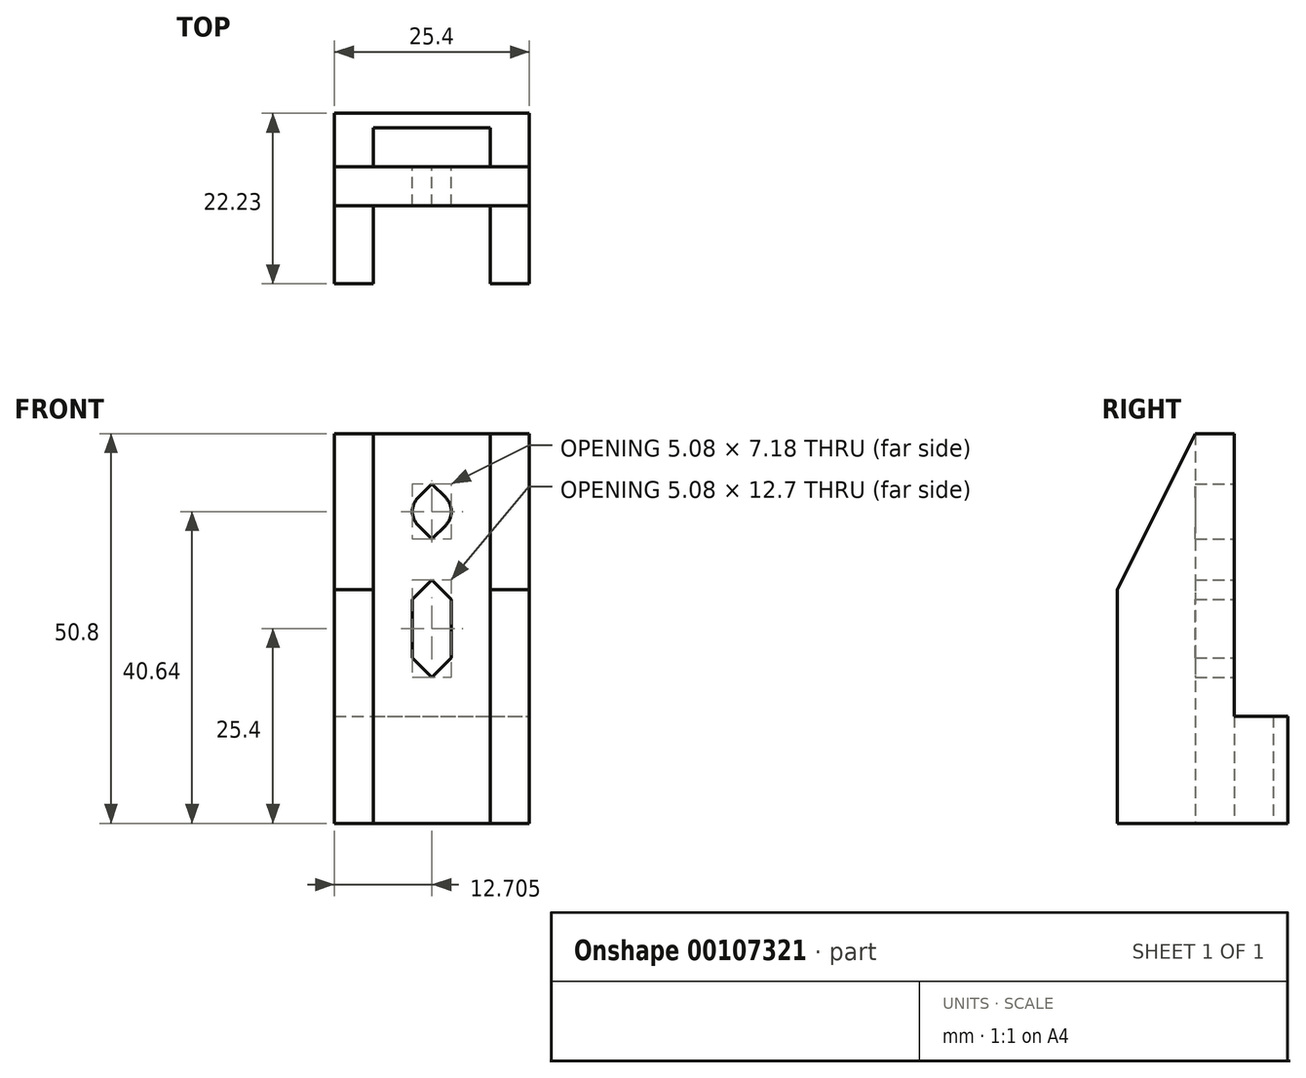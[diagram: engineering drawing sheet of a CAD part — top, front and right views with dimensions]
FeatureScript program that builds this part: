
annotation { "Feature Type Name" : "Feature", "Feature Type Description" : "" }
export const myFeature = defineFeature(function(context is Context, id is Id, definition is map)
    precondition{}
    {
        {
            var Q0;
            Q0=qCreatedBy(makeId("Top.planeOp"),FACE);
            var sketch = newSketch(context, id + "F0", { "sketchPlane" : qUnion([Q0])});
            skLineSegment(sketch, "E0.bottom", {"start": v(-5.07, -11.68) * mm, "end": v(10.17, -11.68) * mm});
            skLineSegment(sketch, "E0.top", {"start": v(-5.07, -6.6) * mm, "end": v(10.17, -6.6) * mm});
            skLineSegment(sketch, "E0.left", {"start": v(-5.07, -11.68) * mm, "end": v(-5.07, -6.6) * mm});
            skLineSegment(sketch, "E0.right", {"start": v(10.17, -11.68) * mm, "end": v(10.17, -6.6) * mm});
            skLineSegment(sketch, "E1.bottom", {"start": v(-10.15, -16.76) * mm, "end": v(15.25, -16.76) * mm});
            skLineSegment(sketch, "E1.top", {"start": v(-10.15, -4.7) * mm, "end": v(15.25, -4.7) * mm});
            skLineSegment(sketch, "E1.left", {"start": v(-10.15, -16.76) * mm, "end": v(-10.15, -4.7) * mm});
            skLineSegment(sketch, "E1.right", {"start": v(15.25, -16.76) * mm, "end": v(15.25, -4.7) * mm});
            skSolve(sketch);
        }
        {
            var Q0;
            Q0=makeQuery(id+"F0.imprint","IMPRINT",FACE,{"disambiguationData":[TD([[makeQuery(id+"F0.imprint","IMPRINT",EDGE,{"derivedFrom":sQuery(id+"F0.wireOp",EDGE,"E0.bottom")}),-1.0]])]});
            extrude(context, id + "F1", {"entities" : qUnion([Q0]), "depth" : 101.6 * mm});
        }
        {
            var Q0;
            Q0=qCreatedBy(makeId("Top.planeOp"),FACE);
            var sketch = newSketch(context, id + "F6", { "sketchPlane" : qUnion([Q0])});
            skLineSegment(sketch, "E2.bottom", {"start": v(-10.15, -16.76) * mm, "end": v(-5.07, -16.76) * mm});
            skLineSegment(sketch, "E2.top", {"start": v(-10.15, -26.92) * mm, "end": v(-5.07, -26.92) * mm});
            skLineSegment(sketch, "E2.left", {"start": v(-10.15, -16.76) * mm, "end": v(-10.15, -26.92) * mm});
            skLineSegment(sketch, "E2.right", {"start": v(-5.07, -16.76) * mm, "end": v(-5.07, -26.92) * mm});
            skLineSegment(sketch, "E3.bottom", {"start": v(15.25, -16.76) * mm, "end": v(10.17, -16.76) * mm});
            skLineSegment(sketch, "E3.top", {"start": v(15.25, -26.92) * mm, "end": v(10.17, -26.92) * mm});
            skLineSegment(sketch, "E3.left", {"start": v(15.25, -16.76) * mm, "end": v(15.25, -26.92) * mm});
            skLineSegment(sketch, "E3.right", {"start": v(10.17, -16.76) * mm, "end": v(10.17, -26.92) * mm});
            skSolve(sketch);
        }
        {
            var Q0;
            Q0 = qSketchRegion(id + "F6", true);
            var Q1;
            Q1=makeQuery(id+"F1.opExtrude","CAP_FACE",FACE,{"disambiguationData":[OSD([sQuery(id+"F0.wireOp",EDGE,"E0.bottom"),sQuery(id+"F0.wireOp",EDGE,"E0.top"),sQuery(id+"F0.wireOp",EDGE,"E0.left"),sQuery(id+"F0.wireOp",EDGE,"E0.right"),sQuery(id+"F0.wireOp",EDGE,"E1.bottom"),sQuery(id+"F0.wireOp",EDGE,"E1.top"),sQuery(id+"F0.wireOp",EDGE,"E1.left"),sQuery(id+"F0.wireOp",EDGE,"E1.right")])],"isStart":false});
            extrude(context, id + "F2", {"entities" : qUnion([Q0]), "operationType" : NewBodyOperationType.ADD, "endBound" : BoundingType.UP_TO_SURFACE, "endBoundEntityFace" : qUnion([Q1]), "depth" : 25.4 * mm});
        }
        {
            var Q0;
            Q0=makeQuery(id+"F2.boolean.opBoolean","MERGE",FACE,{"derivedFrom":[makeQuery(id+"F1.opExtrude","SWEPT_FACE",FACE,{"disambiguationData":[OSD([sQuery(id+"F0.wireOp",EDGE,"E1.right")])]}),makeQuery(id+"F2.opExtrude","SWEPT_FACE",FACE,{"disambiguationData":[OSD([sQuery(id+"F6.wireOp",EDGE,"E3.left")])]})]});
            var sketch = newSketch(context, id + "F3", { "sketchPlane" : qUnion([Q0])});
            skLineSegment(sketch, "E4.bottom", {"start": v(-4.7, 101.6) * mm, "end": v(-11.68, 101.6) * mm});
            skLineSegment(sketch, "E4.top", {"start": v(-4.7, 13.97) * mm, "end": v(-11.68, 13.97) * mm});
            skLineSegment(sketch, "E4.left", {"start": v(-4.7, 101.6) * mm, "end": v(-4.7, 13.97) * mm});
            skLineSegment(sketch, "E4.right", {"start": v(-11.68, 101.6) * mm, "end": v(-11.68, 13.97) * mm});
            skSolve(sketch);
        }
        {
            var Q0;
            Q0 = qSketchRegion(id + "F3", true);
            var Q1;
            Q1=makeQuery(id+"F2.boolean.opBoolean","MERGE",FACE,{"derivedFrom":[makeQuery(id+"F1.opExtrude","SWEPT_FACE",FACE,{"disambiguationData":[OSD([sQuery(id+"F0.wireOp",EDGE,"E1.left")])]}),makeQuery(id+"F2.opExtrude","SWEPT_FACE",FACE,{"disambiguationData":[OSD([sQuery(id+"F6.wireOp",EDGE,"E2.left")])]})]});
            extrude(context, id + "F7", {"entities" : qUnion([Q0]), "operationType" : NewBodyOperationType.REMOVE, "endBound" : BoundingType.UP_TO_SURFACE, "oppositeDirection" : true, "endBoundEntityFace" : qUnion([Q1]), "depth" : 25.4 * mm});
        }
        {
            var Q0;
            Q0=makeQuery(id+"F2.boolean.opBoolean","MERGE",FACE,{"derivedFrom":[makeQuery(id+"F1.opExtrude","SWEPT_FACE",FACE,{"disambiguationData":[OSD([sQuery(id+"F0.wireOp",EDGE,"E1.right")])]}),makeQuery(id+"F2.opExtrude","SWEPT_FACE",FACE,{"disambiguationData":[OSD([sQuery(id+"F6.wireOp",EDGE,"E3.left")])]})]});
            var sketch = newSketch(context, id + "F4", { "sketchPlane" : qUnion([Q0])});
            skLineSegment(sketch, "E5", {"start": v(-26.92, 101.6) * mm, "end": v(-11.68, 101.6) * mm});
            skLineSegment(sketch, "E6", {"start": v(-11.68, 101.6) * mm, "end": v(-11.68, 101.6) * mm});
            skLineSegment(sketch, "E7", {"start": v(-11.68, 50.8) * mm, "end": v(-11.68, 101.6) * mm});
            skLineSegment(sketch, "E8", {"start": v(-16.76, 50.8) * mm, "end": v(-26.92, 30.48) * mm});
            skLineSegment(sketch, "E9", {"start": v(-26.92, 30.48) * mm, "end": v(-26.92, 101.6) * mm});
            skLineSegment(sketch, "E10", {"start": v(-11.68, 50.8) * mm, "end": v(-16.76, 50.8) * mm});
            skSolve(sketch);
        }
        {
            var Q0;
            Q0=makeQuery(id+"F4.imprint","IMPRINT",FACE,{"disambiguationData":[TD([[makeQuery(id+"F4.imprint","IMPRINT",EDGE,{"derivedFrom":sQuery(id+"F4.wireOp",EDGE,"E5")}),-1.0]])]});
            var Q1;
            Q1=makeQuery(id+"F2.boolean.opBoolean","MERGE",FACE,{"derivedFrom":[makeQuery(id+"F1.opExtrude","SWEPT_FACE",FACE,{"disambiguationData":[OSD([sQuery(id+"F0.wireOp",EDGE,"E1.left")])]}),makeQuery(id+"F2.opExtrude","SWEPT_FACE",FACE,{"disambiguationData":[OSD([sQuery(id+"F6.wireOp",EDGE,"E2.left")])]})]});
            extrude(context, id + "F8", {"entities" : qUnion([Q0]), "operationType" : NewBodyOperationType.REMOVE, "endBound" : BoundingType.UP_TO_SURFACE, "oppositeDirection" : true, "endBoundEntityFace" : qUnion([Q1]), "depth" : 25.4 * mm});
        }
        {
            var Q0;
            Q0=makeQuery(id+"F7.boolean.opBoolean","MERGE",FACE,{"derivedFrom":[makeQuery(id+"F1.opExtrude","SWEPT_FACE",FACE,{"disambiguationData":[OSD([sQuery(id+"F0.wireOp",EDGE,"E0.bottom")])]}),makeQuery(id+"F7.opExtrude","SWEPT_FACE",FACE,{"disambiguationData":[OSD([sQuery(id+"F3.wireOp",EDGE,"E4.right")])]})]});
            var sketch = newSketch(context, id + "F9", { "sketchPlane" : qUnion([Q0])});
            skCircle(sketch, "E11", {"center": v(-2.55, 40.64) * mm, "radius": 2.54 * mm});
            skCircle(sketch, "E12", {"center": v(-2.55, 25.4) * mm, "radius": 2.54 * mm});
            skLineSegment(sketch, "E13", {"start": v(-2.55, 40.64) * mm, "end": v(-2.55, 25.4) * mm, "construction": true});
            skLineSegment(sketch, "E14", {"start": v(-15.25, 40.64) * mm, "end": v(-2.55, 40.64) * mm, "construction": true});
            skLineSegment(sketch, "E15", {"start": v(10.15, 40.64) * mm, "end": v(-2.55, 40.64) * mm, "construction": true});
            skSolve(sketch);
        }
        {
            var Q0;
            Q0 = qSketchRegion(id + "F9", true);
            extrude(context, id + "F5", {"entities" : qUnion([Q0]), "operationType" : NewBodyOperationType.REMOVE, "endBound" : BoundingType.UP_TO_NEXT, "oppositeDirection" : true, "depth" : 25.4 * mm});
        }
        {
            var Q0;
            Q0=makeQuery(id+"F7.boolean.opBoolean","MERGE",FACE,{"derivedFrom":[makeQuery(id+"F1.opExtrude","SWEPT_FACE",FACE,{"disambiguationData":[OSD([sQuery(id+"F0.wireOp",EDGE,"E0.bottom")])]}),makeQuery(id+"F7.opExtrude","SWEPT_FACE",FACE,{"disambiguationData":[OSD([sQuery(id+"F3.wireOp",EDGE,"E4.right")])]})]});
            var sketch = newSketch(context, id + "F10", { "sketchPlane" : qUnion([Q0])});
            skLineSegment(sketch, "E16.bottom", {"start": v(-0.01, 29.21) * mm, "end": v(-5.1, 29.21) * mm, "construction": true});
            skLineSegment(sketch, "E16.top", {"start": v(-0.01, 21.6) * mm, "end": v(-5.1, 21.6) * mm, "construction": true});
            skLineSegment(sketch, "E16.left", {"start": v(-0.01, 29.21) * mm, "end": v(-0.01, 21.6) * mm});
            skLineSegment(sketch, "E16.right", {"start": v(-5.1, 29.21) * mm, "end": v(-5.1, 21.6) * mm});
            skPoint(sketch, "E16.middle", {"position": v(-2.55, 25.4) * mm});
            skLineSegment(sketch, "E17", {"start": v(-5.1, 29.21) * mm, "end": v(-2.55, 31.75) * mm});
            skLineSegment(sketch, "E18", {"start": v(-2.55, 31.75) * mm, "end": v(-2.55, 31.75) * mm});
            skLineSegment(sketch, "E19", {"start": v(-0.01, 29.21) * mm, "end": v(-2.55, 31.75) * mm});
            skLineSegment(sketch, "E20", {"start": v(-0.01, 21.6) * mm, "end": v(-2.55, 19.05) * mm});
            skLineSegment(sketch, "E21", {"start": v(-2.55, 19.05) * mm, "end": v(-2.55, 19.05) * mm});
            skLineSegment(sketch, "E22", {"start": v(-2.55, 19.05) * mm, "end": v(-5.1, 21.59) * mm});
            skLineSegment(sketch, "E23", {"start": v(-4.35, 42.44) * mm, "end": v(-2.55, 44.23) * mm});
            skLineSegment(sketch, "E24", {"start": v(-2.55, 44.23) * mm, "end": v(-0.76, 42.44) * mm});
            skLineSegment(sketch, "E25", {"start": v(-4.35, 38.84) * mm, "end": v(-2.55, 37.05) * mm});
            skLineSegment(sketch, "E26", {"start": v(-2.55, 37.05) * mm, "end": v(-0.76, 38.84) * mm});
            skLineSegment(sketch, "E27", {"start": v(-4.35, 42.44) * mm, "end": v(-0.76, 42.44) * mm});
            skLineSegment(sketch, "E28", {"start": v(-0.76, 38.84) * mm, "end": v(-4.35, 38.84) * mm});
            skSolve(sketch);
        }
        {
            var Q0;
            Q0 = qSketchRegion(id + "F10", true);
            var Q1;
            Q1=makeQuery(id+"F1.opExtrude","SWEPT_FACE",FACE,{"disambiguationData":[OSD([sQuery(id+"F0.wireOp",EDGE,"E1.bottom")])]});
            extrude(context, id + "F11", {"entities" : qUnion([Q0]), "operationType" : NewBodyOperationType.REMOVE, "endBound" : BoundingType.UP_TO_SURFACE, "oppositeDirection" : true, "endBoundEntityFace" : qUnion([Q1]), "depth" : 25.4 * mm});
        }
    });
